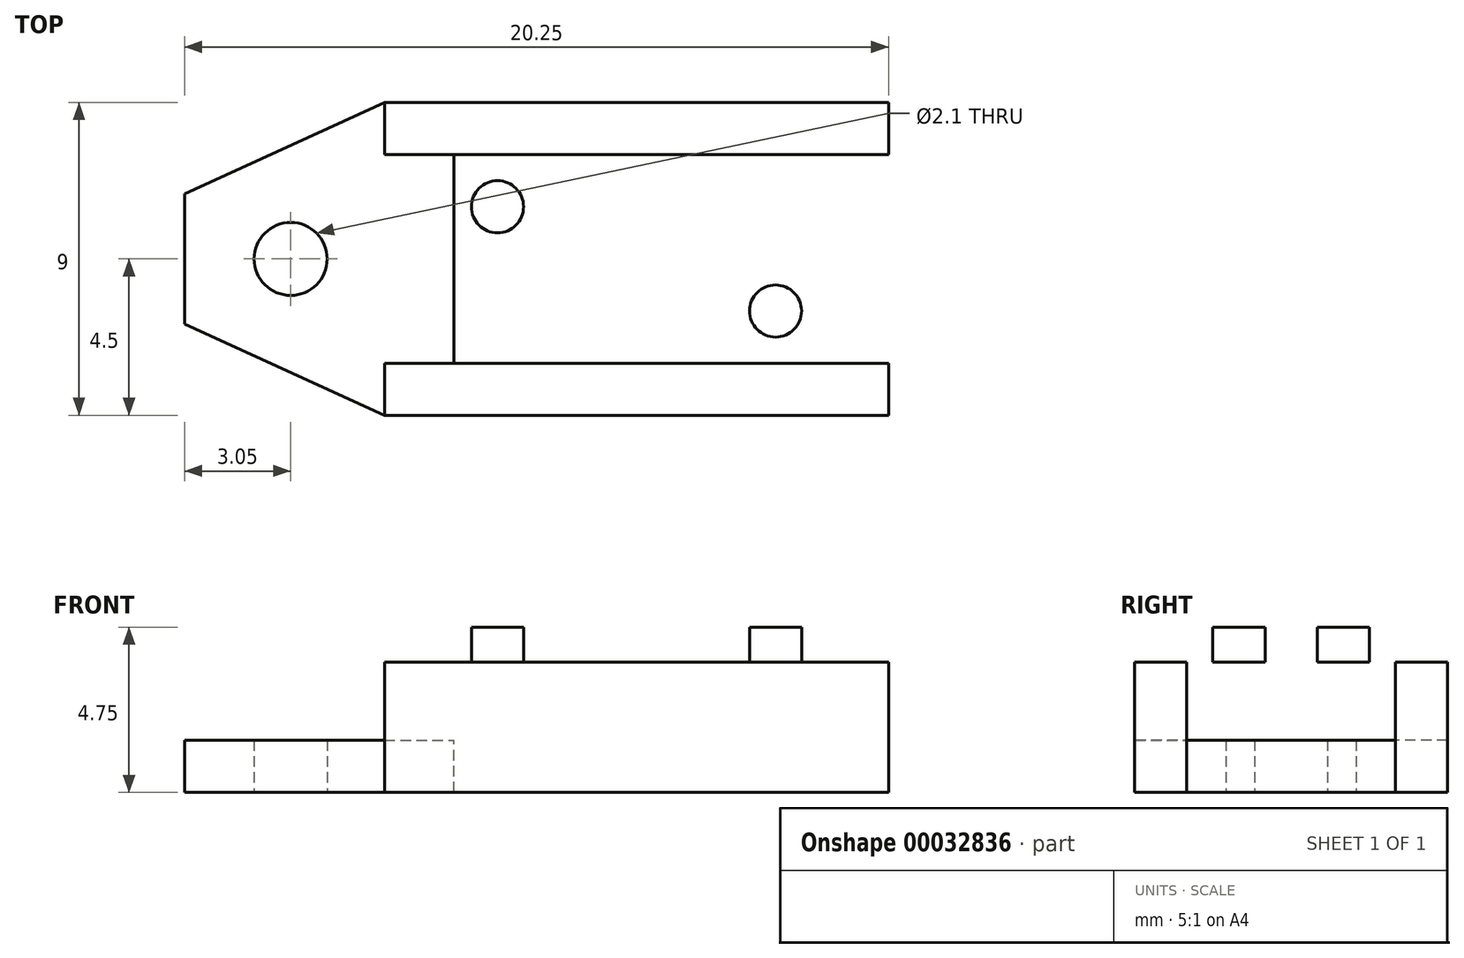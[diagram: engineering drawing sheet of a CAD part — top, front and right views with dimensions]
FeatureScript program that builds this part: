
annotation { "Feature Type Name" : "Feature", "Feature Type Description" : "" }
export const myFeature = defineFeature(function(context is Context, id is Id, definition is map)
    precondition{}
    {
        {
            var Q0;
            Q0=qCreatedBy(makeId("Top.planeOp"),FACE);
            var sketch = newSketch(context, id + "F0", { "sketchPlane" : qUnion([Q0])});
            skLineSegment(sketch, "E0.rect.bottom", {"start": v(6.25, 3.5) * mm, "end": v(-6.25, 3.5) * mm});
            skLineSegment(sketch, "E0.rect.top", {"start": v(6.25, -3.5) * mm, "end": v(-6.25, -3.5) * mm});
            skLineSegment(sketch, "E0.rect.left", {"start": v(6.25, 3.5) * mm, "end": v(6.25, -3.5) * mm});
            skLineSegment(sketch, "E0.rect.right", {"start": v(-6.25, 3.5) * mm, "end": v(-6.25, -3.5) * mm});
            skPoint(sketch, "E0.rect.middle", {"position": v(0, 0) * mm});
            skLineSegment(sketch, "E1.0", {"start": v(7.25, 4.5) * mm, "end": v(-7.25, 4.5) * mm});
            skLineSegment(sketch, "E1.1", {"start": v(7.25, 4.5) * mm, "end": v(7.25, -4.5) * mm});
            skLineSegment(sketch, "E1.2", {"start": v(7.25, -4.5) * mm, "end": v(-7.25, -4.5) * mm});
            skLineSegment(sketch, "E1.3", {"start": v(-7.25, 4.5) * mm, "end": v(-7.25, -4.5) * mm});
            skSolve(sketch);
        }
        {
            var Q0;
            Q0=makeQuery(id+"F0.imprint","IMPRINT",FACE,{"disambiguationData":[TD([[makeQuery(id+"F0.imprint","IMPRINT",EDGE,{"derivedFrom":sQuery(id+"F0.wireOp",EDGE,"E0.rect.bottom")}),-1.0]])]});
            extrude(context, id + "F1", {"entities" : qUnion([Q0]), "depth" : 2 * mm});
        }
        {
            var Q0;
            Q0=makeQuery(id+"F0.imprint","IMPRINT",FACE,{"disambiguationData":[TD([[makeQuery(id+"F0.imprint","IMPRINT",EDGE,{"derivedFrom":sQuery(id+"F0.wireOp",EDGE,"E0.rect.bottom")}),1.0]])]});
            var Q1;
            Q1=makeQuery(id+"F0.imprint","IMPRINT",FACE,{"disambiguationData":[TD([[makeQuery(id+"F0.imprint","IMPRINT",EDGE,{"derivedFrom":sQuery(id+"F0.wireOp",EDGE,"E0.rect.bottom")}),-1.0]])]});
            extrude(context, id + "F2", {"entities" : qUnion([Q0, Q1]), "operationType" : NewBodyOperationType.ADD, "oppositeDirection" : true, "depth" : 1 * mm});
        }
        {
            var Q0;
            Q0=makeQuery(id+"F2.opExtrude","CAP_FACE",FACE,{"disambiguationData":[OSD([sQuery(id+"F0.wireOp",EDGE,"E1.0"),sQuery(id+"F0.wireOp",EDGE,"E1.1"),sQuery(id+"F0.wireOp",EDGE,"E1.2"),sQuery(id+"F0.wireOp",EDGE,"E1.3")])],"isStart":false});
            var sketch = newSketch(context, id + "F3", { "sketchPlane" : qUnion([Q0])});
            skCircle(sketch, "E2", {"center": v(-4, 1.5) * mm, "radius": 0.75 * mm});
            skLineSegment(sketch, "E3", {"start": v(0, 0) * mm, "end": v(1.3, 0) * mm, "construction": true});
            skLineSegment(sketch, "E4", {"start": v(0, 0) * mm, "end": v(0, 1.35) * mm, "construction": true});
            skCircle(sketch, "E5.MirrorC", {"center": v(4, 1.5) * mm, "radius": 0.75 * mm});
            skCircle(sketch, "E6.MirrorC", {"center": v(4, -1.5) * mm, "radius": 0.75 * mm});
            skCircle(sketch, "E7.MirrorC", {"center": v(-4, -1.5) * mm, "radius": 0.75 * mm});
            skSolve(sketch);
        }
        {
            var Q0;
            Q0=makeQuery(id+"F3.imprint","IMPRINT",FACE,{"disambiguationData":[TD([[makeQuery(id+"F3.imprint","IMPRINT",EDGE,{"derivedFrom":sQuery(id+"F3.wireOp",EDGE,"E2")}),1.0]])]});
            var Q1;
            Q1=makeQuery(id+"F3.imprint","IMPRINT",FACE,{"disambiguationData":[TD([[makeQuery(id+"F3.imprint","IMPRINT",EDGE,{"derivedFrom":sQuery(id+"F3.wireOp",EDGE,"E5.MirrorC")}),-1.0]])]});
            var Q2;
            Q2=makeQuery(id+"F3.imprint","IMPRINT",FACE,{"disambiguationData":[TD([[makeQuery(id+"F3.imprint","IMPRINT",EDGE,{"derivedFrom":sQuery(id+"F3.wireOp",EDGE,"E6.MirrorC")}),1.0]])]});
            var Q3;
            Q3=makeQuery(id+"F3.imprint","IMPRINT",FACE,{"disambiguationData":[TD([[makeQuery(id+"F3.imprint","IMPRINT",EDGE,{"derivedFrom":sQuery(id+"F3.wireOp",EDGE,"E7.MirrorC")}),-1.0]])]});
            extrude(context, id + "F4", {"entities" : qUnion([Q0, Q1, Q2, Q3]), "operationType" : NewBodyOperationType.REMOVE, "endBound" : BoundingType.THROUGH_ALL, "oppositeDirection" : true, "depth" : 25 * mm});
        }
        {
            var Q0;
            Q0=makeQuery(id+"F2.opExtrude","CAP_FACE",FACE,{"disambiguationData":[OSD([sQuery(id+"F0.wireOp",EDGE,"E1.0"),sQuery(id+"F0.wireOp",EDGE,"E1.1"),sQuery(id+"F0.wireOp",EDGE,"E1.2"),sQuery(id+"F0.wireOp",EDGE,"E1.3")])],"isStart":false});
            var sketch = newSketch(context, id + "F5", { "sketchPlane" : qUnion([Q0])});
            skLineSegment(sketch, "E8.bottom", {"start": v(-7.25, 4.5) * mm, "end": v(7.25, 4.5) * mm});
            skLineSegment(sketch, "E8.top", {"start": v(-7.25, 3) * mm, "end": v(7.25, 3) * mm});
            skLineSegment(sketch, "E8.left", {"start": v(-7.25, 4.5) * mm, "end": v(-7.25, 3) * mm});
            skLineSegment(sketch, "E8.right", {"start": v(7.25, 4.5) * mm, "end": v(7.25, 3) * mm});
            skLineSegment(sketch, "E9", {"start": v(0, 0) * mm, "end": v(3.29, 0) * mm, "construction": true});
            skLineSegment(sketch, "E10.MirrorCS", {"start": v(7.25, -4.5) * mm, "end": v(7.25, -3) * mm});
            skLineSegment(sketch, "E11.MirrorCS", {"start": v(-7.25, -4.5) * mm, "end": v(-7.25, -3) * mm});
            skLineSegment(sketch, "E12.MirrorCS", {"start": v(-7.25, -3) * mm, "end": v(7.25, -3) * mm});
            skLineSegment(sketch, "E13.MirrorCS", {"start": v(-7.25, -4.5) * mm, "end": v(7.25, -4.5) * mm});
            skSolve(sketch);
        }
        {
            var Q0;
            Q0 = qSketchRegion(id + "F5", true);
            extrude(context, id + "F6", {"entities" : qUnion([Q0]), "operationType" : NewBodyOperationType.ADD, "depth" : 3.75 * mm});
        }
        {
            var Q0;
            Q0=makeQuery(id+"F6.opExtrude","CAP_FACE",FACE,{"disambiguationData":[OSD([sQuery(id+"F5.wireOp",EDGE,"E8.bottom"),sQuery(id+"F5.wireOp",EDGE,"E8.top"),sQuery(id+"F5.wireOp",EDGE,"E8.left"),sQuery(id+"F5.wireOp",EDGE,"E8.right")])],"isStart":false});
            var sketch = newSketch(context, id + "F7", { "sketchPlane" : qUnion([Q0])});
            skCircle(sketch, "E14", {"center": v(-9.95, 0) * mm, "radius": 1.05 * mm});
            skPoint(sketch, "E15.0", {"position": v(-7.25, -4.5) * mm});
            skPoint(sketch, "E16.0", {"position": v(-7.25, 4.5) * mm});
            skLineSegment(sketch, "E17.0", {"start": v(-7.25, -4.5) * mm, "end": v(-7.25, 4.5) * mm});
            skLineSegment(sketch, "E18", {"start": v(-7.25, -4.5) * mm, "end": v(-13, -1.88) * mm});
            skLineSegment(sketch, "E19", {"start": v(-13, 1.88) * mm, "end": v(-7.25, 4.5) * mm});
            skLineSegment(sketch, "E20", {"start": v(-13, 1.88) * mm, "end": v(-13, -1.88) * mm});
            skPoint(sketch, "E21.orphan", {"position": v(-17.11, 0) * mm});
            skLineSegment(sketch, "E22", {"start": v(-7.25, -4.5) * mm, "end": v(-5.25, -4.5) * mm});
            skLineSegment(sketch, "E23", {"start": v(-5.25, -4.5) * mm, "end": v(-5.25, 4.5) * mm});
            skLineSegment(sketch, "E24", {"start": v(-5.25, 4.5) * mm, "end": v(-7.25, 4.5) * mm});
            skSolve(sketch);
        }
        {
            var Q0;
            Q0 = qSketchRegion(id + "F7", true);
            extrude(context, id + "F8", {"entities" : qUnion([Q0]), "operationType" : NewBodyOperationType.ADD, "oppositeDirection" : true, "depth" : 1.5 * mm});
        }
    });
